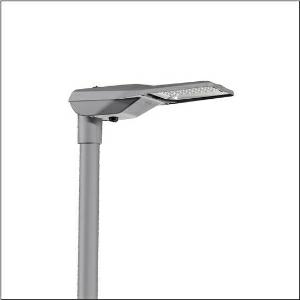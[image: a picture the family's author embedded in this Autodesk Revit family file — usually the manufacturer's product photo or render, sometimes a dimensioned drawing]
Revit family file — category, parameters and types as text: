
# Revit family: streetlight_sl_21_iq_mini___p0_5a_5xe2v31y08hb_0b7f
name_source: partatom
category: Lighting Fixtures
units: mm (PartAtom-declared; Revit-internal decimal feet)

## family parameters
Cut with Voids When Loaded = No
Host = Face
Light Source = No
Part Type = Normal
Room Calculation Point = No
Round Connector Dimension = Use Diameter
Shared = No

## types (1)
- --- (1 x LED, 9580 lm, 71 W, 3000K)
    Apparent Load = 71 VA
    CIE Flux Codes = 37 73 96 100 100
    Color Rendering = 70
    Color Temperature = 3000K
    Default Elevation = 1800 mm
    Description = Streetlight SL 21 iQ mini, mast luminaire, primary light control with lens, of PMMA, primary optical cover: cover, of toughened safety glass, transparent, light distribution: P0.5a, light emission: direct distribution, primary light characteristic: asymmetric, installation type: post-top, side-entry, LED, High Power LED, rated luminous flux: 9.580lm, luminous efficacy: 135lm/W, light colour: 730, colour temperature: 3000K, control gear: iQ-Street Remote, D4i with power reduction, control: pre-setting: logarithmic dimming characteristic, Street-Remote, Auto-Match, Temp-Guard, Lumen-Switch, Night-Set, Smart-Wire, Light-Fading, Desk-Remote (wireless, voltage-free reading and setting of iQ features in the workshop via application-optimized NFC function/RFID function), optimised constant luminous flux control (CLO 2.0), mains connection: 220..240V, AC, 50/60Hz, start of lifetime: 71W, end of service life: 75W, reduction: 30W, luminaire housing, of diecast aluminium, powder-coated, Siteco® metallic grey (DB 702S), corrosivity category C5 mid according to DIN EN ISO 12944, please order mast flange separately, inclination adjustable: 0°, 5°, 10°, 15°, sealing non-destructively replaceable, multi-level sealing system, length: 628mm, width: 235mm, height: 110mm, mast flange for spigot size: 42mm (side-entry): 5XC10008XM4, 60/48mm (side-entry/post-top): 5XC10108XM2, 76/60mm (side-entry/post-top): 5XC10108XM1, mounting height: 4..8m, Smart Interface below and above, protection rating (complete): IP66, insulation class (complete): insulation class II (safety insulation), certification: CE, ENEC, ENEC+, VDE, impact resistance: IK10, permissible operating ambient temperature for outdoor applications: -40..+50°C, standard-compliant lighting for roads and squares, packaging unit: 1 piece

Light Distribution: P0.5a
    Height = 110 mm
    Lamp = 1 x LED
    Lamp Light Flux = 9580 lm
    Lamp Power = 71 W
    Lamp count = 1
    Length = 625 mm
    Luminous efficacy = 135 lm/W
    Manufacturer = Siteco
    ModVariant = No
    Model = 5XE2V31Y08HB
    Number of Poles = 1
    OnlyDefault = Yes
    Power Factor = 1
    Product Name = Streetlight SL 21 iQ mini | P0.5a
    Product group = mast luminaire | pylon top
    ProductGroupID = 6100
    Protection Class = Protection class II
    Protection Degree = IP 66
    RLX_Detail_Level = 1
    RLX_Emergency_Light_Flux = 0 lm
    RLX_Emergency_Type = 0
    RLX_Emergency_Type_DB = No
    RlxData = <blob elided: 26153 chars, md5=51e40410>
    Socket = socket
    Standby Power = 0 W
    System Light Flux = 9580 lm
    System Power = 71 W
    Type Comments = factory setting: luminous flux: 100 % | dim-lin: 254 | 716 mA
    Type Image = l_1003514.jpg
    URL = http://relux.com
    VarID = @adj_070556
    Voltage = 0 V
    Weight = 0.00 kg
    Width = 234 mm

## geometry (parser evidence)
native form markers: Blend x4, Sweep x10
no freeform markers — native parametric forms only
